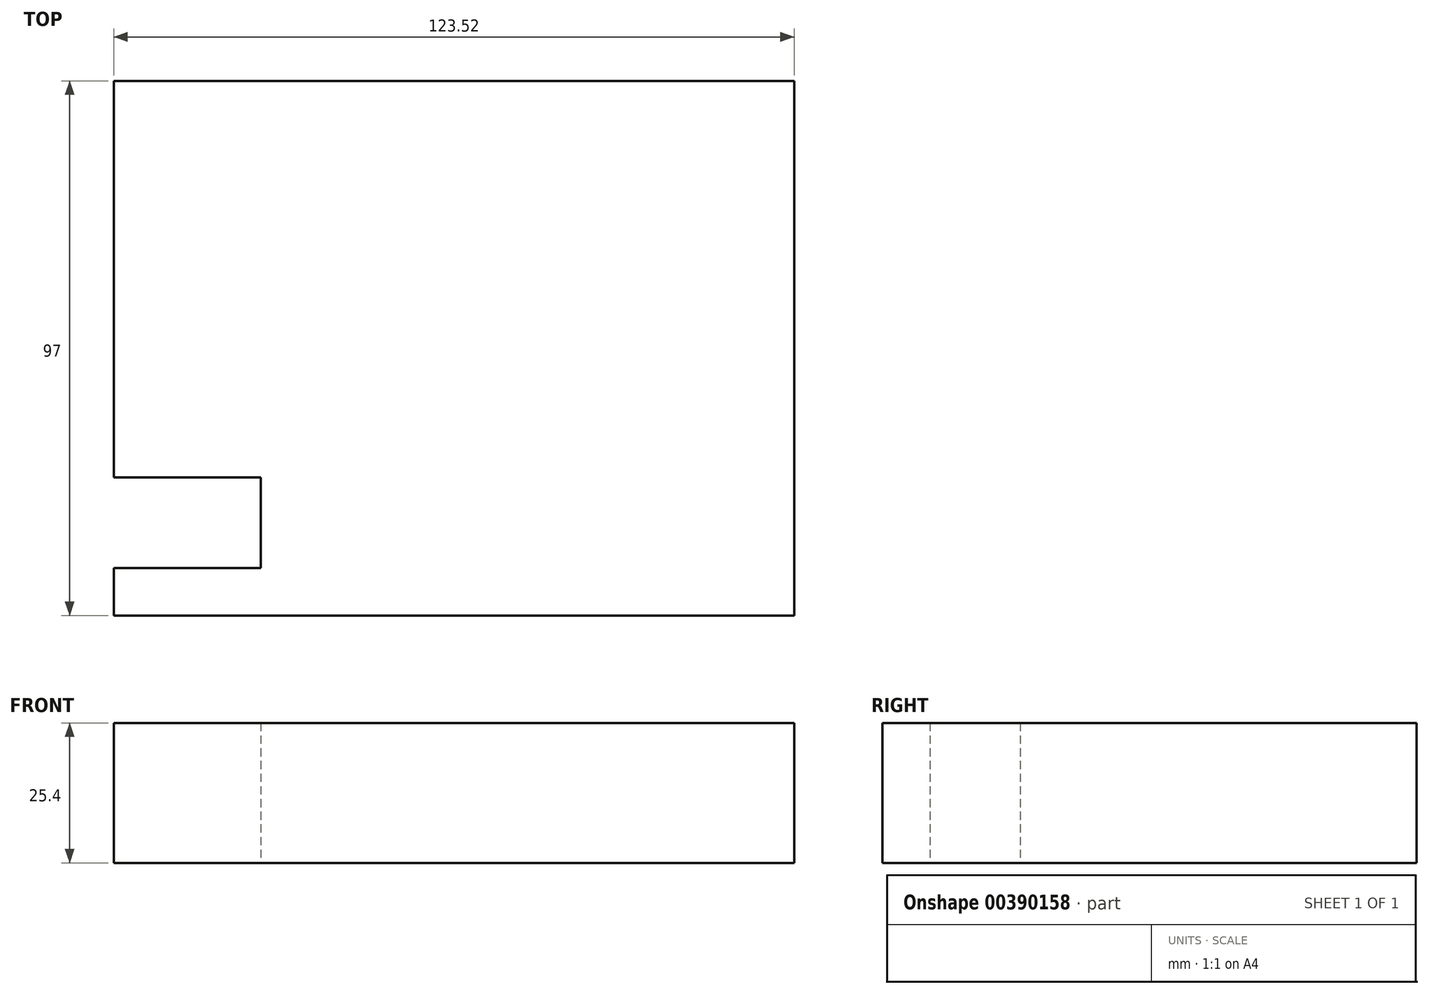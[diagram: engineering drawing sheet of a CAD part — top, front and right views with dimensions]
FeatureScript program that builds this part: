
annotation { "Feature Type Name" : "Feature", "Feature Type Description" : "" }
export const myFeature = defineFeature(function(context is Context, id is Id, definition is map)
    precondition{}
    {
        {
            var Q0;
            Q0=qCreatedBy(makeId("Top.planeOp"),FACE);
            var sketch = newSketch(context, id + "F0", { "sketchPlane" : qUnion([Q0])});
            skLineSegment(sketch, "E0.bottom", {"start": v(0, 57.65) * mm, "end": v(0, 57.65) * mm});
            skLineSegment(sketch, "E0.top", {"start": v(0, 17.53) * mm, "end": v(0, 17.53) * mm});
            skLineSegment(sketch, "E0.left", {"start": v(0, 57.65) * mm, "end": v(0, 17.53) * mm});
            skLineSegment(sketch, "E0.right", {"start": v(0, 57.65) * mm, "end": v(0, 17.53) * mm});
            skLineSegment(sketch, "E1.bottom", {"start": v(-2.04, 11.9) * mm, "end": v(-44.62, 11.9) * mm});
            skLineSegment(sketch, "E1.top", {"start": v(-2.04, -4.54) * mm, "end": v(-44.62, -4.54) * mm});
            skLineSegment(sketch, "E1.left", {"start": v(-2.04, 11.9) * mm, "end": v(-2.04, -4.54) * mm});
            skLineSegment(sketch, "E1.right", {"start": v(-44.62, 11.9) * mm, "end": v(-44.62, -4.54) * mm});
            skLineSegment(sketch, "E2.bottom", {"start": v(-28.71, -13.17) * mm, "end": v(94.8, -13.17) * mm});
            skLineSegment(sketch, "E2.top", {"start": v(-28.71, 83.83) * mm, "end": v(94.8, 83.83) * mm});
            skLineSegment(sketch, "E2.left", {"start": v(-28.71, -13.17) * mm, "end": v(-28.71, 83.83) * mm});
            skLineSegment(sketch, "E2.right", {"start": v(94.8, -13.17) * mm, "end": v(94.8, 83.83) * mm});
            skSolve(sketch);
        }
        {
            var Q0;
            {var subQ1=sQuery(id+"F0.wireOp",EDGE,"E1.left");Q0=makeQuery(id+"F0.imprint","IMPRINT",FACE,{"disambiguationData":[TD([[makeQuery(id+"F0.imprint","IMPRINT",EDGE,{"derivedFrom":subQ1}),1.0]])]});}
            extrude(context, id + "F1", {"entities" : qUnion([Q0]), "depth" : 25.4 * mm});
        }
    });
